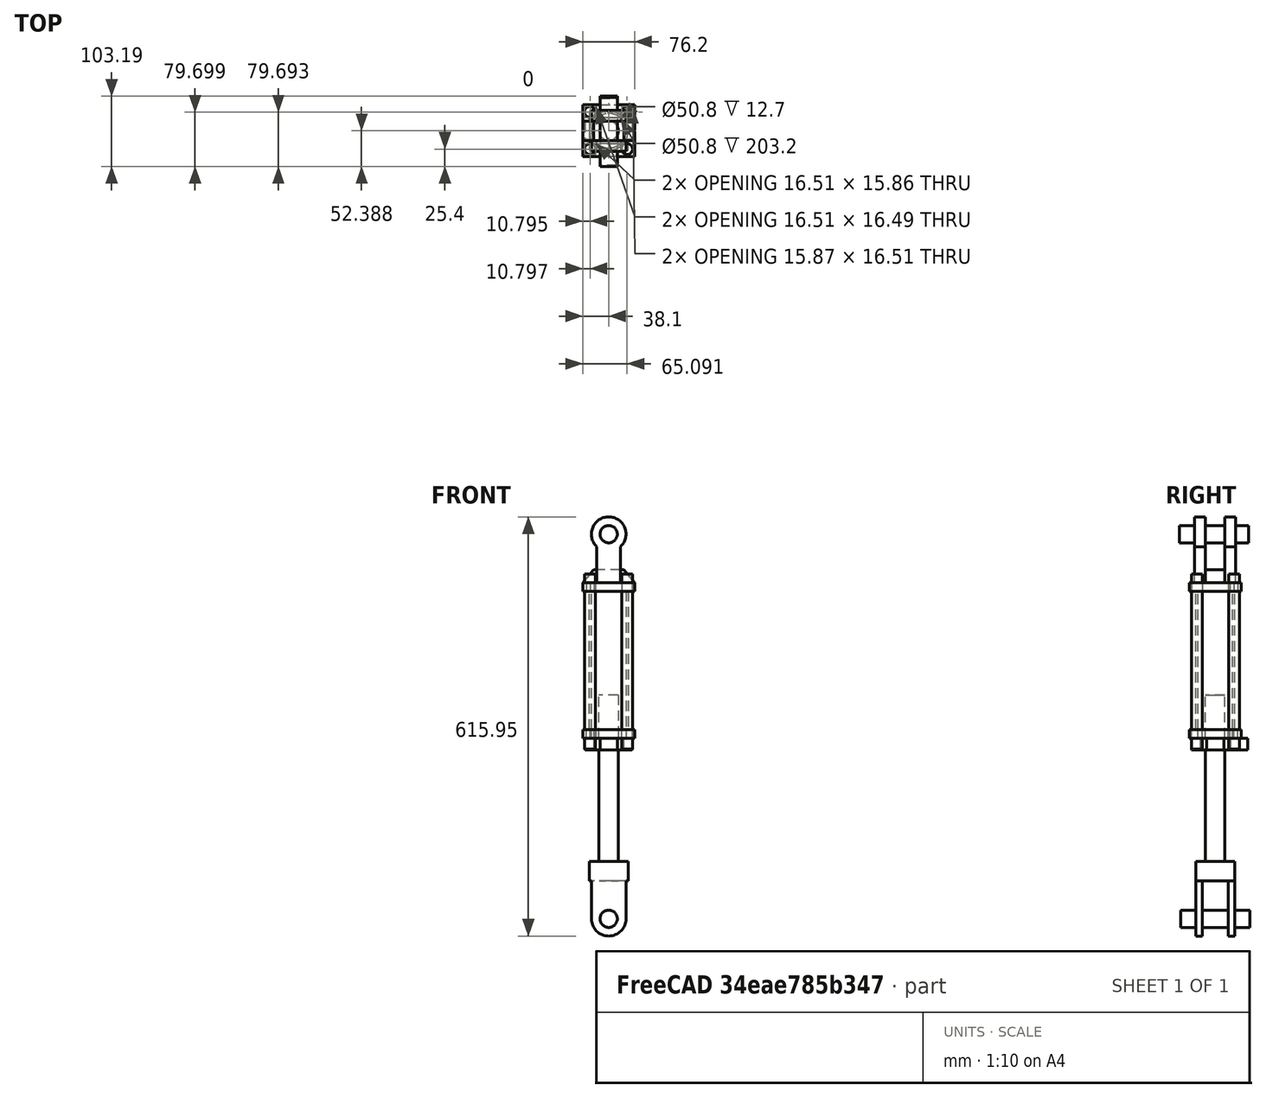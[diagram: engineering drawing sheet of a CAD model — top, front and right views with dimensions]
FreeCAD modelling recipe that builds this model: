
FCSTD DOCUMENT  (FreeCAD 0.17R13519 (Git))
Label: cylinder new extended
License: CreativeCommons Attribution
LicenseURL: http://creativecommons.org/licenses/by/4.0/
objects: Sketcher::SketchObject×10, PartDesign::Pad×10, PartDesign::FeatureBase×9, PartDesign::Body×4, PartDesign::LinearPattern×2, Part::FeaturePython×2, Part::MultiFuse×2, App::FeaturePython×2, TechDraw::DrawProjGroupItem×2, TechDraw::DrawViewDimension×2, Part::Cylinder×1, TechDraw::DrawSVGTemplate×1, TechDraw::DrawProjGroup×1, TechDraw::DrawViewImage×1, TechDraw::DrawViewAnnotation×1, TechDraw::DrawPage×1
note: 50 computed .brp shape members not serialized (recipe doc carries the construction recipe); baked Part::Feature solids carry a one-line shape summary decoded from their .brp

FEATURE [Sketcher::SketchObject] Sketch
  MapMode = 5
  Support = -> [XY_Plane]
  sketch-geometry (12):
    g0: LineSegment StartX=-38.1 StartY=38.1 StartZ=0 EndX=38.1 EndY=38.1 EndZ=0
    g1: LineSegment StartX=38.1 StartY=38.1 StartZ=0 EndX=38.1 EndY=-38.1 EndZ=0
    g2: LineSegment StartX=38.1 StartY=-38.1 StartZ=0 EndX=-38.1 EndY=-38.1 EndZ=0
    g3: LineSegment StartX=-38.1 StartY=-38.1 StartZ=0 EndX=-38.1 EndY=38.1 EndZ=0
    g4: LineSegment [constr] StartX=-26.9875 StartY=26.9875 StartZ=0 EndX=26.9875 EndY=26.9875 EndZ=0
    g5: LineSegment [constr] StartX=26.9875 StartY=26.9875 StartZ=0 EndX=26.9875 EndY=-26.9875 EndZ=0
    g6: LineSegment [constr] StartX=26.9875 StartY=-26.9875 StartZ=0 EndX=-26.9875 EndY=-26.9875 EndZ=0
    g7: LineSegment [constr] StartX=-26.9875 StartY=-26.9875 StartZ=0 EndX=-26.9875 EndY=26.9875 EndZ=0
    g8: Circle CenterX=-26.9875 CenterY=26.9875 CenterZ=0 NormalX=0 NormalY=0 NormalZ=1 AngleXU=0 Radius=7.9375
    g9: Circle CenterX=26.9875 CenterY=26.9875 CenterZ=0 NormalX=0 NormalY=0 NormalZ=1 AngleXU=0 Radius=7.9375
    g10: Circle CenterX=-26.9875 CenterY=-26.9875 CenterZ=0 NormalX=0 NormalY=0 NormalZ=1 AngleXU=0 Radius=7.9375
    g11: Circle CenterX=26.9875 CenterY=-26.9875 CenterZ=0 NormalX=0 NormalY=0 NormalZ=1 AngleXU=0 Radius=7.9375
  constraints (32):
    c: Coincident(g0,g1)
    c: Coincident(g1,g2)
    c: Coincident(g2,g3)
    c: Coincident(g3,g0)
    c: Horizontal(g0)
    c: Horizontal(g2)
    c: Vertical(g1)
    c: Vertical(g3)
    c: Equal(g2,g1)
    c: Symmetric(g1,g2,g-2)
    c: DistanceX(g2,g2) = 76.2
    c: Symmetric(g0,g1,g-1)
    c: Coincident(g4,g5)
    c: Coincident(g5,g6)
    c: Coincident(g6,g7)
    c: Coincident(g7,g4)
    c: Horizontal(g4)
    c: Horizontal(g6)
    c: Vertical(g5)
    c: Vertical(g7)
    c: Symmetric(g5,g4,g-1)
    c: Symmetric(g5,g6,g-2)
    c: DistanceX(g6,g6) = 53.975
    c: Equal(g6,g5)
    c: Coincident(g8,g4)
    c: Coincident(g9,g4)
    c: Coincident(g10,g6)
    c: Coincident(g11,g5)
    c: Radius(g11) = 7.9375
    c: Equal(g11,g9)
    c: Equal(g11,g8)
    c: Equal(g11,g10)
FEATURE [Sketcher::SketchObject] Sketch001
  MapMode = 3
  Placement = pos=(0,0,12.7) rot=(1,0,0;1.5708rad)
  sketch-geometry (4):
    g0: LineSegment StartX=-38.1 StartY=0 StartZ=0 EndX=38.1 EndY=0 EndZ=0
    g1: LineSegment StartX=38.1 StartY=0 StartZ=0 EndX=22.225 EndY=19.05 EndZ=0
    g2: LineSegment StartX=22.225 StartY=19.05 StartZ=0 EndX=-22.225 EndY=19.05 EndZ=0
    g3: LineSegment StartX=-22.225 StartY=19.05 StartZ=0 EndX=-38.1 EndY=0 EndZ=0
  constraints (12):
    c: PointOnObject(g0,g-1)
    c: Horizontal(g0)
    c: Coincident(g0,g1)
    c: Coincident(g1,g2)
    c: Coincident(g2,g3)
    c: Coincident(g3,g0)
    c: Horizontal(g2)
    c: Symmetric(g2,g1,g-2)
    c: Symmetric(g0,g0,g-2)
    c: DistanceY(g0,g2) = 19.05
    c: DistanceX(g2,g2) = 44.45
    c: DistanceX(g0,g0) = 76.2
FEATURE [PartDesign::Pad] Pad
  Length = 12.7
  Length2 = 100.076
  Profile = -> Sketch
  Type = 0
FEATURE [PartDesign::Pad] Pad001
  BaseFeature = -> Pad
  Length = 28.575
  Length2 = 100.076
  Midplane = true
  Profile = -> Sketch001
  Type = 0
FEATURE [Sketcher::SketchObject] Sketch002
  MapMode = 5
  Placement = pos=(0,-14.2875,0) rot=(1,0,0;1.5708rad)
  Support = -> [Pad001]
  sketch-geometry (5):
    g0: LineSegment StartX=-17.4625 StartY=0 StartZ=0 EndX=17.4625 EndY=0 EndZ=0
    g1: LineSegment StartX=17.4625 StartY=0 StartZ=0 EndX=17.4625 EndY=65.3749 EndZ=0
    g2: LineSegment StartX=-17.4625 StartY=65.3749 StartZ=0 EndX=-17.4625 EndY=0 EndZ=0
    g3: Circle CenterX=0 CenterY=83.82 CenterZ=0 NormalX=0 NormalY=0 NormalZ=1 AngleXU=0 Radius=12.7
    g4: ArcOfCircle CenterX=0 CenterY=83.82 CenterZ=0 NormalX=0 NormalY=0 NormalZ=1 AngleXU=0 Radius=25.4 StartAngle=5.47043 EndAngle=10.2375
  constraints (15):
    c: PointOnObject(g0,g-1)
    c: Horizontal(g0)
    c: Coincident(g0,g1)
    c: Vertical(g1)
    c: Coincident(g2,g0)
    c: Vertical(g2)
    c: PointOnObject(g4,g-2)
    c: DistanceX(g0,g0) = 34.925
    c: Symmetric(g0,g0,g-2)
    c: Radius(g3) = 12.7
    c: Radius(g4) = 25.4
    c: Coincident(g2,g4)
    c: Coincident(g1,g4)
    c: Coincident(g3,g4)
    c: DistanceY(g-1,g3) = 83.82
FEATURE [PartDesign::Pad] Pad002
  BaseFeature = -> Pad001
  Length = 15.875
  Length2 = 100.076
  Profile = -> Sketch002
  Type = 0
FEATURE [PartDesign::LinearPattern] LinearPattern
  Direction = -> Sketch002 [N_Axis]
  Length = 44.45
  Occurrences = 2
  Originals = -> [Pad002]
  Reversed = true
FEATURE [Sketcher::SketchObject] Sketch003
  MapMode = 5
  Placement = pos=(0,0,0) rot=(1,0,0;3.14159rad)
  Support = -> [LinearPattern]
  sketch-geometry (2):
    g0: Circle CenterX=0 CenterY=0 CenterZ=0 NormalX=0 NormalY=0 NormalZ=1 AngleXU=0 Radius=28.575
    g1: Circle CenterX=0 CenterY=0 CenterZ=0 NormalX=0 NormalY=0 NormalZ=1 AngleXU=0 Radius=25.4
  constraints (4):
    c: Coincident(g0,g-1)
    c: Radius(g0) = 28.575
    c: Coincident(g1,g-1)
    c: Radius(g1) = 25.4
FEATURE [PartDesign::Pad] Pad003
  BaseFeature = -> LinearPattern
  Length = 203.2
  Length2 = 100.076
  Profile = -> Sketch003
  Type = 0
FEATURE [Sketcher::SketchObject] Sketch004
  MapMode = 5
  Placement = pos=(0,0,-203.2) rot=(1,0,0;3.14159rad)
  Support = -> [Pad003]
  sketch-geometry (13):
    g0: LineSegment StartX=-38.1 StartY=38.1 StartZ=0 EndX=38.1 EndY=38.1 EndZ=0
    g1: LineSegment StartX=38.1 StartY=38.1 StartZ=0 EndX=38.1 EndY=-38.1 EndZ=0
    g2: LineSegment StartX=38.1 StartY=-38.1 StartZ=0 EndX=-38.1 EndY=-38.1 EndZ=0
    g3: LineSegment StartX=-38.1 StartY=-38.1 StartZ=0 EndX=-38.1 EndY=38.1 EndZ=0
    g4: LineSegment [constr] StartX=-26.9875 StartY=26.9875 StartZ=0 EndX=26.9875 EndY=26.9875 EndZ=0
    g5: LineSegment [constr] StartX=26.9875 StartY=26.9875 StartZ=0 EndX=26.9875 EndY=-26.9875 EndZ=0
    g6: LineSegment [constr] StartX=26.9875 StartY=-26.9875 StartZ=0 EndX=-26.9875 EndY=-26.9875 EndZ=0
    g7: LineSegment [constr] StartX=-26.9875 StartY=-26.9875 StartZ=0 EndX=-26.9875 EndY=26.9875 EndZ=0
    g8: Circle CenterX=-26.9875 CenterY=26.9875 CenterZ=0 NormalX=0 NormalY=0 NormalZ=1 AngleXU=0 Radius=7.9375
    g9: Circle CenterX=26.9875 CenterY=26.9875 CenterZ=0 NormalX=0 NormalY=0 NormalZ=1 AngleXU=0 Radius=7.9375
    g10: Circle CenterX=-26.9875 CenterY=-26.9875 CenterZ=0 NormalX=0 NormalY=0 NormalZ=1 AngleXU=0 Radius=7.9375
    g11: Circle CenterX=26.9875 CenterY=-26.9875 CenterZ=0 NormalX=0 NormalY=0 NormalZ=1 AngleXU=0 Radius=7.9375
    g12: Circle CenterX=0 CenterY=0 CenterZ=0 NormalX=0 NormalY=0 NormalZ=1 AngleXU=0 Radius=25.4
  constraints (34):
    c: Coincident(g0,g1)
    c: Coincident(g1,g2)
    c: Coincident(g2,g3)
    c: Coincident(g3,g0)
    c: Horizontal(g0)
    c: Horizontal(g2)
    c: Vertical(g1)
    c: Vertical(g3)
    c: Equal(g2,g1)
    c: Symmetric(g1,g2,g-2)
    c: DistanceX(g2,g2) = 76.2
    c: Symmetric(g0,g1,g-1)
    c: Coincident(g4,g5)
    c: Coincident(g5,g6)
    c: Coincident(g6,g7)
    c: Coincident(g7,g4)
    c: Horizontal(g4)
    c: Horizontal(g6)
    c: Vertical(g5)
    c: Vertical(g7)
    c: Symmetric(g5,g4,g-1)
    c: Symmetric(g5,g6,g-2)
    c: DistanceX(g6,g6) = 53.975
    c: Equal(g6,g5)
    c: Coincident(g8,g4)
    c: Coincident(g9,g4)
    c: Coincident(g10,g6)
    c: Coincident(g11,g5)
    c: Radius(g11) = 7.9375
    c: Equal(g11,g9)
    c: Equal(g11,g8)
    c: Equal(g11,g10)
    c: Coincident(g12,g-1)
    c: Radius(g12) = 25.4
FEATURE [PartDesign::Pad] Pad004
  BaseFeature = -> Pad003
  Length = 12.7
  Length2 = 100.076
  Profile = -> Sketch004
  Type = 0
FEATURE [Sketcher::SketchObject] Sketch005
  MapMode = 5
  Placement = pos=(0,0,-215.9) rot=(1,0,0;3.14159rad)
  Support = -> [Pad004]
  sketch-geometry (17):
    g0: ArcOfCircle CenterX=0 CenterY=0 CenterZ=0 NormalX=0 NormalY=0 NormalZ=1 AngleXU=0 Radius=25.4 StartAngle=0.523599 EndAngle=1.0472
    g1: Circle CenterX=0 CenterY=0 CenterZ=0 NormalX=0 NormalY=0 NormalZ=1 AngleXU=0 Radius=14.2875
    g2: LineSegment StartX=-12.7 StartY=34.697 StartZ=0 EndX=12.7 EndY=34.697 EndZ=0
    g3: LineSegment StartX=12.7 StartY=34.697 StartZ=0 EndX=12.7 EndY=21.997 EndZ=0
    g4: LineSegment StartX=-12.7 StartY=21.997 StartZ=0 EndX=-12.7 EndY=34.697 EndZ=0
    g5: LineSegment StartX=34.697 StartY=12.7 StartZ=0 EndX=21.997 EndY=12.7 EndZ=0
    g6: LineSegment StartX=21.997 StartY=-12.7 StartZ=0 EndX=34.697 EndY=-12.7 EndZ=0
    g7: LineSegment StartX=34.697 StartY=-12.7 StartZ=0 EndX=34.697 EndY=12.7 EndZ=0
    g8: LineSegment StartX=-34.697 StartY=12.7 StartZ=0 EndX=-21.997 EndY=12.7 EndZ=0
    g9: LineSegment StartX=-21.997 StartY=-12.7 StartZ=0 EndX=-34.697 EndY=-12.7 EndZ=0
    g10: LineSegment StartX=-34.697 StartY=-12.7 StartZ=0 EndX=-34.697 EndY=12.7 EndZ=0
    g11: LineSegment StartX=-12.7 StartY=-47.397 StartZ=0 EndX=12.7 EndY=-47.397 EndZ=0
    g12: LineSegment StartX=12.7 StartY=-47.397 StartZ=0 EndX=12.7 EndY=-21.997 EndZ=0
    g13: LineSegment StartX=-12.7 StartY=-21.997 StartZ=0 EndX=-12.7 EndY=-47.397 EndZ=0
    g14: ArcOfCircle CenterX=0 CenterY=0 CenterZ=0 NormalX=0 NormalY=0 NormalZ=1 AngleXU=0 Radius=25.4 StartAngle=3.66519 EndAngle=4.18879
    g15: ArcOfCircle CenterX=0 CenterY=0 CenterZ=0 NormalX=0 NormalY=0 NormalZ=1 AngleXU=0 Radius=25.4 StartAngle=5.23599 EndAngle=5.75959
    g16: ArcOfCircle CenterX=0 CenterY=0 CenterZ=0 NormalX=0 NormalY=0 NormalZ=1 AngleXU=0 Radius=25.4 StartAngle=2.0944 EndAngle=2.61799
  constraints (46):
    c: Coincident(g0,g-1)
    c: Coincident(g1,g-1)
    c: Radius(g0) = 25.4
    c: Radius(g1) = 14.2875
    c: Coincident(g2,g3)
    c: Coincident(g4,g2)
    c: Horizontal(g2)
    c: Vertical(g3)
    c: Vertical(g4)
    c: Coincident(g6,g7)
    c: Coincident(g7,g5)
    c: Horizontal(g5)
    c: Horizontal(g6)
    c: Vertical(g7)
    c: Coincident(g9,g10)
    c: Coincident(g10,g8)
    c: Horizontal(g8)
    c: Horizontal(g9)
    c: Vertical(g10)
    c: Coincident(g11,g12)
    c: Coincident(g13,g11)
    c: Horizontal(g11)
    c: Vertical(g12)
    c: Vertical(g13)
    c: PointOnObject(g12,g0)
    c: Equal(g11,g7)
    c: Equal(g7,g2)
    c: Equal(g2,g10)
    c: DistanceX(g11,g11) = 25.4
    c: Symmetric(g11,g11,g-2)
    c: PointOnObject(g6,g0)
    c: PointOnObject(g9,g0)
    c: Equal(g5,g3)
    c: Equal(g3,g8)
    c: DistanceX(g6,g6) = 12.7
    c: DistanceY(g12,g12) = 25.4
    c: PointOnObject(g0,g5)
    c: Equal(g0,g14)
    c: PointOnObject(g16,g8)
    c: Coincident(g0,g14)
    c: Equal(g14,g15)
    c: PointOnObject(g15,g12)
    c: Coincident(g14,g15)
    c: Equal(g0,g16)
    c: Coincident(g0,g3)
    c: Coincident(g0,g16)
FEATURE [PartDesign::Pad] Pad005
  BaseFeature = -> Pad004
  Length = 17.145
  Length2 = 100.076
  Profile = -> Sketch005
  Type = 0
FEATURE [PartDesign::Body] Body
  Group = -> [Sketch,Pad,Sketch001,Pad001,Sketch002,Pad002,LinearPattern,Sketch003,Pad003,Sketch004,Pad004,Sketch005,Pad005]
  Origin = -> Origin
  Tip = -> Pad005
FEATURE [Sketcher::SketchObject] Sketch006
  MapMode = 5
  Support = -> [XY_Plane001]
  sketch-geometry (1):
    g0: Circle CenterX=0 CenterY=0 CenterZ=0 NormalX=0 NormalY=0 NormalZ=1 AngleXU=0 Radius=14.2875
  constraints (2):
    c: Coincident(g-1,g0)
    c: Radius(g0) = 14.2875
FEATURE [PartDesign::Pad] Pad006
  Length = 273.05
  Length2 = 100.076
  Profile = -> Sketch006
  Reversed = true
  Type = 0
FEATURE [Sketcher::SketchObject] Sketch007
  MapMode = 5
  Placement = pos=(0,0,-273.05) rot=(1,0,0;3.14159rad)
  Support = -> [Pad006]
  sketch-geometry (4):
    g0: LineSegment StartX=-28.575 StartY=28.575 StartZ=0 EndX=28.575 EndY=28.575 EndZ=0
    g1: LineSegment StartX=28.575 StartY=28.575 StartZ=0 EndX=28.575 EndY=-28.575 EndZ=0
    g2: LineSegment StartX=28.575 StartY=-28.575 StartZ=0 EndX=-28.575 EndY=-28.575 EndZ=0
    g3: LineSegment StartX=-28.575 StartY=-28.575 StartZ=0 EndX=-28.575 EndY=28.575 EndZ=0
  constraints (12):
    c: Coincident(g0,g1)
    c: Coincident(g1,g2)
    c: Coincident(g2,g3)
    c: Coincident(g3,g0)
    c: Horizontal(g0)
    c: Horizontal(g2)
    c: Vertical(g1)
    c: Vertical(g3)
    c: Symmetric(g1,g0,g-1)
    c: Symmetric(g2,g1,g-2)
    c: Equal(g2,g1)
    c: DistanceX(g2,g2) = 57.15
FEATURE [PartDesign::Pad] Pad007
  BaseFeature = -> Pad006
  Length = 28.575
  Length2 = 100.076
  Profile = -> Sketch007
  Reversed = true
  Type = 0
FEATURE [Sketcher::SketchObject] Sketch008
  MapMode = 5
  Placement = pos=(0,-28.575,0) rot=(1,0,0;1.5708rad)
  Support = -> [Pad007]
  sketch-geometry (5):
    g0: LineSegment StartX=-25.4 StartY=-247.65 StartZ=0 EndX=25.4 EndY=-247.65 EndZ=0
    g1: LineSegment StartX=25.4 StartY=-247.65 StartZ=0 EndX=25.4 EndY=-328.93 EndZ=0
    g2: LineSegment StartX=-25.4 StartY=-328.93 StartZ=0 EndX=-25.4 EndY=-247.65 EndZ=0
    g3: Circle CenterX=0 CenterY=-328.93 CenterZ=0 NormalX=0 NormalY=0 NormalZ=1 AngleXU=0 Radius=12.7
    g4: ArcOfCircle CenterX=0 CenterY=-328.93 CenterZ=0 NormalX=0 NormalY=0 NormalZ=1 AngleXU=0 Radius=25.4 StartAngle=3.14159 EndAngle=6.28319
  constraints (15):
    c: Coincident(g0,g1)
    c: Coincident(g2,g0)
    c: Horizontal(g0)
    c: Vertical(g1)
    c: Vertical(g2)
    c: PointOnObject(g3,g-2)
    c: Radius(g3) = 12.7
    c: Coincident(g4,g3)
    c: Radius(g4) = 25.4
    c: Symmetric(g0,g0,g-2)
    c: DistanceY(g3,g0) = 81.28
    c: Coincident(g4,g2)
    c: Coincident(g4,g1)
    c: DistanceX(g0,g0) = 50.8
    c: DistanceY(g0,g-1) = 247.65
FEATURE [PartDesign::Pad] Pad008
  BaseFeature = -> Pad007
  Length = 9.525
  Length2 = 100.076
  Profile = -> Sketch008
  Reversed = true
  Type = 0
FEATURE [PartDesign::LinearPattern] LinearPattern001
  Direction = -> Sketch008 [N_Axis]
  Length = 47.625
  Occurrences = 2
  Originals = -> [Pad008]
  Reversed = true
FEATURE [PartDesign::Body] Body001
  Group = -> [Sketch006,Pad006,Sketch007,Pad007,Sketch008,Pad008,LinearPattern001]
  Origin = -> Origin001
  Placement = pos=(0,0,-152.4) rot=(0,0,1;0rad)
  Tip = -> LinearPattern001
FEATURE [Sketcher::SketchObject] Sketch010
  MapMode = 5
  Support = -> [XY_Plane003]
  sketch-geometry (1):
    g0: Circle CenterX=26.9875 CenterY=-26.9875 CenterZ=0 NormalX=0 NormalY=0 NormalZ=1 AngleXU=0 Radius=7.9375
  constraints (3):
    c: Radius(g0) = 7.9375
    c: DistanceX(g0) = 26.9875
    c: DistanceY(g0) = -26.9875
FEATURE [PartDesign::Pad] Pad010
  Length = 257.175
  Length2 = 100.076
  Profile = -> Sketch010
  Reversed = true
  Type = 0
FEATURE [PartDesign::FeatureBase] BaseFeature
  BaseFeature = -> Pad010
FEATURE [PartDesign::Body] Body002
  BaseFeature = -> Pad010
  Group = -> [BaseFeature]
  Origin = -> Origin002
  Tip = -> BaseFeature
FEATURE [Part::FeaturePython] Array  # Draft array (typed FeaturePython)
  Angle = 360
  ArrayType = 0
  Axis = (0,0,1)
  Base = -> Body002
  Center = (0,0,0)
  Fuse = false
  IntervalAxis = (0,0,0)
  IntervalX = (-54.61,0,0)
  IntervalY = (0,54.61,0)
  IntervalZ = (0,0,0)
  NumberPolar = 1
  NumberX = 2
  NumberY = 2
  NumberZ = 1
  Placement = pos=(0,0,25.4) rot=(0,0,1;0rad)
FEATURE [PartDesign::FeatureBase] BaseFeature001  label="Unnamed001"
  BaseFeature = -> Pad010
FEATURE [Part::MultiFuse] Fusion
  Placement = pos=(0,-133.032,0) rot=(0,0,1;0rad)
  Refine = true
  Shapes = -> [Body,Body001,Array]
FEATURE [PartDesign::FeatureBase] BaseFeature002  label="Unnamed002"
  BaseFeature = -> Pad010
FEATURE [PartDesign::FeatureBase] BaseFeature003  label="Unnamed003"
  BaseFeature = -> Pad010
FEATURE [PartDesign::FeatureBase] BaseFeature004  label="Unnamed004"
  BaseFeature = -> Pad010
FEATURE [Part::Cylinder] Cylinder
  Angle = 360
  AttacherType = Attacher::AttachEngine3D
  Height = 101.6
  Placement = pos=(0,-83.82,83.82) rot=(1,0,0;1.5708rad)
  Radius = 12.7
FEATURE [Part::FeaturePython] Clone  label="Cylinder001"  # Draft clone (typed FeaturePython)
  AttacherType = Attacher::AttachEngine3D
  Fuse = false
  Objects = -> [Cylinder]
  Placement = pos=(0,-82.2325,-481.33) rot=(1,0,0;1.5708rad)
  Scale = (1,1,1)
FEATURE [PartDesign::FeatureBase] BaseFeature005  label="Unnamed005"
  BaseFeature = -> Pad010
FEATURE [PartDesign::FeatureBase] BaseFeature006  label="Unnamed006"
  BaseFeature = -> Pad010
FEATURE [PartDesign::FeatureBase] BaseFeature007  label="Unnamed007"
  BaseFeature = -> Pad010
FEATURE [App::FeaturePython] circularEdgeConstraint01  # a2plus constraint (typed FeaturePython)
  Object1 = Cylinder
  Object2 = Fusion
  SubElement1 = Face1
  SubElement2 = Face54
  Type = circularEdge
  directionConstraint = 1
  lockRotation = false
  offset = -63.5
FEATURE [App::FeaturePython] circularEdgeConstraint02  # a2plus constraint (typed FeaturePython)
  Object1 = Clone
  Object2 = Fusion
  SubElement1 = Face1
  SubElement2 = Face101
  Type = circularEdge
  directionConstraint = 0
  lockRotation = false
  offset = -79.375
FEATURE [Part::MultiFuse] Fusion001
  Refine = true
  Shapes = -> [Cylinder,Clone,Fusion]
FEATURE [PartDesign::FeatureBase] BaseFeature008
  BaseFeature = -> Fusion001
FEATURE [PartDesign::Body] Body003
  BaseFeature = -> Fusion001
  Group = -> [BaseFeature008]
  Origin = -> Origin003
  Placement = pos=(0,-100,0) rot=(0,0,1;0rad)
  Tip = -> BaseFeature008
FEATURE [TechDraw::DrawSVGTemplate] Template
  EditableTexts = Designed_by_Name=Designed by Name; Drawing_number=Drawing number; FC-Date=Date; FC-SC=Scale; FC-SH=Sheet; FC-Title=Title; Subtitle=Subtitle; Weight=Weight
  Height = 210
  Orientation = 1
  Width = 297
FEATURE [TechDraw::DrawProjGroupItem] ProjItem
  CoarseView = false
  Direction = (0,-1,0)
  Focus = 100
  HardHidden = false
  IsoCount = 0
  IsoHidden = false
  IsoVisible = false
  LockPosition = false
  Perspective = false
  Rotation = 0
  RotationVector = (0,0,-1)
  ScaleType = 0
  SeamHidden = false
  SeamVisible = false
  SmoothHidden = false
  SmoothVisible = false
  Source = -> [Body003]
  Type = 0
  X = 0
  Y = 0
FEATURE [TechDraw::DrawProjGroupItem] ProjItem001
  CoarseView = false
  Direction = (-1,0,0)
  Focus = 100
  HardHidden = false
  IsoCount = 0
  IsoHidden = false
  IsoVisible = false
  LockPosition = false
  Perspective = false
  Rotation = 0
  RotationVector = (0,0,-1)
  Scale = 0.25
  ScaleType = 2
  SeamHidden = false
  SeamVisible = false
  SmoothHidden = false
  SmoothVisible = false
  Source = -> [Body003]
  Type = 5
  X = 0
  Y = 40.7969
FEATURE [TechDraw::DrawProjGroup] ProjGroup
  Anchor = -> ProjItem
  AutoDistribute = true
  CubeDirs = (6) [(-1,0,-6.12323e-17),(0,-1,0),(-6.12323e-17,0,1),(0,1,0),(6.12323e-17,0,-1),(1,0,6.12323e-17)]
  CubeRotations = (6) [(-6.12323e-17,0,-1),(-6.12323e-17,0,-1),(0,1,0),(6.12323e-17,0,1),(0,-1,0),(-6.12323e-17,0,-1)]
  LockPosition = false
  ProjectionType = 0
  Rotation = 0
  Scale = 0.25
  ScaleType = 2
  Source = -> [Body003]
  Views = -> [ProjItem,ProjItem001]
  X = 98.6022
  Y = 139.619
  spacingX = 15
  spacingY = 15
FEATURE [TechDraw::DrawViewImage] Image
  Height = 1000
  ImageFile = <path> Reference.png
  LockPosition = false
  Rotation = 0
  Scale = 1.23
  ScaleType = 2
  Width = 1200
  X = 83.7629
  Y = 66.6359
FEATURE [TechDraw::DrawViewAnnotation] Annotation
  Font = Rosewood Std Regular
  LineSpace = 80
  LockPosition = false
  MaxWidth = -1
  Rotation = 0
  ScaleType = 0
  Text = Keywords: | Cylinder retracted length  | from center to center of pins: 16.25inch" | Cylinder extended: 22.25inch" | Common 2"(bore diameter)  | x 6"(stroke length) dimension cylinders
  TextSize = 4
  TextStyle = 0
  X = 213.876
  Y = 87.714
FEATURE [TechDraw::DrawViewDimension] Dimension
  FormatSpec = %.2f
  LockPosition = false
  MeasureType = 1
  References2D = -> [ProjItem]
  Rotation = 0
  ScaleType = 0
  Type = 0
  X = 5.30809
  Y = -23.3556
FEATURE [TechDraw::DrawViewDimension] Dimension001
  FormatSpec = %.2f
  LockPosition = false
  MeasureType = 1
  References2D = -> [ProjItem]
  Rotation = 0
  ScaleType = 0
  Type = 2
  X = 92.6
  Y = 0.940534
FEATURE [TechDraw::DrawPage] Page001  label="Cylinder Specs"
  KeepUpdated = true
  ProjectionType = 0
  Template = -> Template
  Views = -> [ProjGroup,Image,Annotation,Dimension,Dimension001]
note: 1 file-system path scrubbed to <path> (originals preserved in the JSON sidecar)
